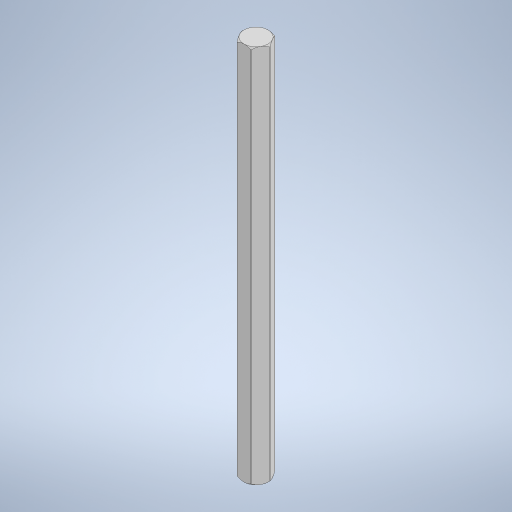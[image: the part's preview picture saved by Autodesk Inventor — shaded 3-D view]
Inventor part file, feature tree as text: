
AUTODESK INVENTOR PART (.ipt)
format: ipt  version: 2023 (Build 270158000, 158)  size: 268,800 bytes
history: native  units: in
note: dims shown in document units (in); Inventor stores cm internally (conversion verified against a paired STEP export)
features: other x2, mirror x1
ambient origin geometry x8: Origin, YZ Plane, XZ Plane, XY Plane, X Axis, Y Axis, Z Axis, Center Point
bodies: Solid1 (feature_tree)
feature tree (3):
  other  "Table"
  other  "REX Shaft (8mm Diameter, 110mm Length)-01"
  mirror  "Mirror1"
